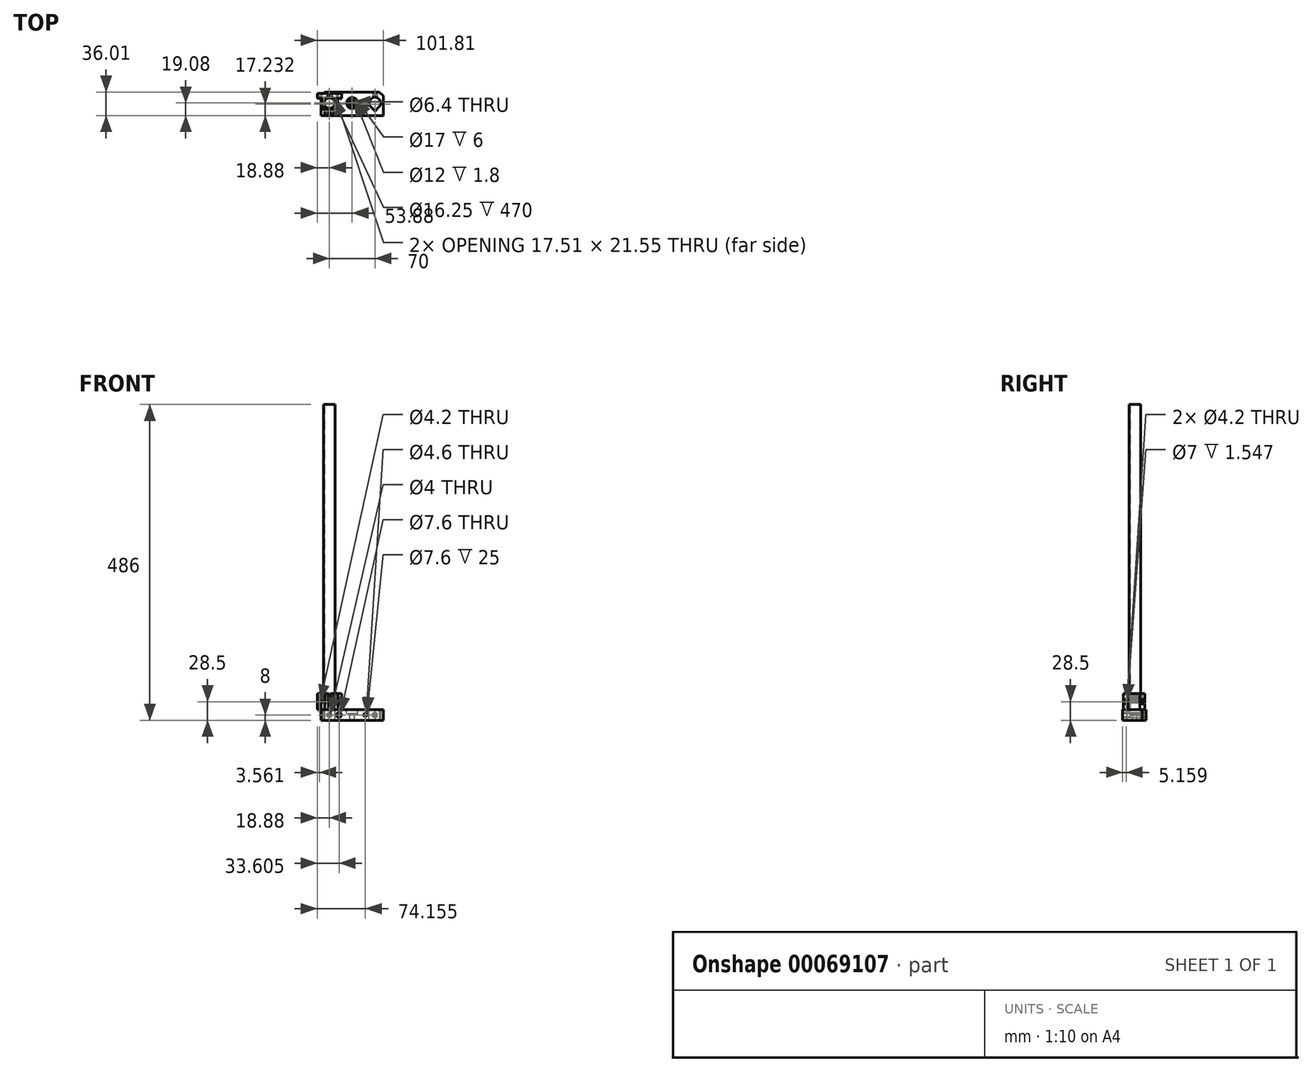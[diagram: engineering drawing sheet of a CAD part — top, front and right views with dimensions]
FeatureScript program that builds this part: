
annotation { "Feature Type Name" : "Feature", "Feature Type Description" : "" }
export const myFeature = defineFeature(function(context is Context, id is Id, definition is map)
    precondition{}
    {
        {
            var Q0;
            Q0=qCreatedBy(makeId("Top.planeOp"),FACE);
            var sketch = newSketch(context, id + "F0", { "sketchPlane" : qUnion([Q0])});
            skCircle(sketch, "E0", {"center": v(0, 0) * mm, "radius": 8.93 * mm, "construction": true});
            skLineSegment(sketch, "E1", {"start": v(0, 0) * mm, "end": v(0, 15.23) * mm, "construction": true});
            skLineSegment(sketch, "E2", {"start": v(0, 15.23) * mm, "end": v(18.88, 15.23) * mm});
            skLineSegment(sketch, "E3", {"start": v(18.88, 15.23) * mm, "end": v(18.88, 7.23) * mm});
            skLineSegment(sketch, "E4", {"start": v(18.88, 7.23) * mm, "end": v(11.08, 7.23) * mm});
            skArc(sketch, "E5", {"start": v(3.5, -8.54) * mm, "mid": v(9.05, 1.78) * mm, "end": v(0, 9.23) * mm});
            skArc(sketch, "E6", {"start": v(7, -11.22) * mm, "mid": v(12.91, -2.85) * mm, "end": v(11.08, 7.23) * mm});
            skLineSegment(sketch, "E7", {"start": v(1.5, -10.21) * mm, "end": v(1.5, -18.02) * mm});
            skLineSegment(sketch, "E8", {"start": v(1.5, -18.02) * mm, "end": v(7, -18.02) * mm});
            skLineSegment(sketch, "E9", {"start": v(7, -18.02) * mm, "end": v(7, -11.22) * mm});
            skLineSegment(sketch, "E10", {"start": v(1.5, -10.21) * mm, "end": v(3.5, -8.54) * mm});
            skLineSegment(sketch, "E11.MirrorCS", {"start": v(-1.5, -10.21) * mm, "end": v(-3.5, -8.54) * mm});
            skLineSegment(sketch, "E12.MirrorCS", {"start": v(-7, -18.02) * mm, "end": v(-7, -11.22) * mm});
            skLineSegment(sketch, "E13.MirrorCS", {"start": v(-1.5, -18.02) * mm, "end": v(-7, -18.02) * mm});
            skLineSegment(sketch, "E14.MirrorCS", {"start": v(-18.88, 7.22) * mm, "end": v(-11.08, 7.22) * mm});
            skLineSegment(sketch, "E15.MirrorCS", {"start": v(-18.88, 15.23) * mm, "end": v(-18.88, 7.22) * mm});
            skLineSegment(sketch, "E16.MirrorCS", {"start": v(0, 15.23) * mm, "end": v(-18.88, 15.22) * mm});
            skLineSegment(sketch, "E17.MirrorCS", {"start": v(-1.5, -10.21) * mm, "end": v(-1.5, -18.02) * mm});
            skArc(sketch, "E18.MirrorCS", {"start": v(-7, -11.22) * mm, "mid": v(-12.91, -2.85) * mm, "end": v(-11.08, 7.22) * mm});
            skArc(sketch, "E19.MirrorCS", {"start": v(-3.5, -8.54) * mm, "mid": v(-9.05, 1.78) * mm, "end": v(0, 9.23) * mm});
            skLineSegment(sketch, "E20.bottom", {"start": v(-10.53, 0.4) * mm, "end": v(-7.32, 0.4) * mm});
            skLineSegment(sketch, "E20.top", {"start": v(-10.53, -0.4) * mm, "end": v(-7.32, -0.4) * mm});
            skLineSegment(sketch, "E20.left", {"start": v(-10.53, 0.4) * mm, "end": v(-10.53, -0.4) * mm});
            skLineSegment(sketch, "E20.right", {"start": v(-7.33, 0.4) * mm, "end": v(-7.33, -0.4) * mm});
            skPoint(sketch, "E20.middle", {"position": v(-8.93, 0) * mm});
            skLineSegment(sketch, "E21.1.0", {"start": v(-10.27, -2.34) * mm, "end": v(-10.06, -3.11) * mm});
            skLineSegment(sketch, "E21.1.1", {"start": v(-10.27, -2.34) * mm, "end": v(-7.18, -1.5) * mm});
            skLineSegment(sketch, "E21.1.2", {"start": v(-7.18, -1.5) * mm, "end": v(-6.97, -2.28) * mm});
            skLineSegment(sketch, "E21.1.3", {"start": v(-10.06, -3.11) * mm, "end": v(-6.97, -2.28) * mm});
            skLineSegment(sketch, "E21.2.0", {"start": v(-9.31, -4.92) * mm, "end": v(-8.91, -5.6) * mm});
            skLineSegment(sketch, "E21.2.1", {"start": v(-9.31, -4.92) * mm, "end": v(-6.54, -3.32) * mm});
            skLineSegment(sketch, "E21.2.2", {"start": v(-6.54, -3.32) * mm, "end": v(-6.14, -4) * mm});
            skLineSegment(sketch, "E21.2.3", {"start": v(-8.91, -5.6) * mm, "end": v(-6.14, -4) * mm});
            skLineSegment(sketch, "E21.3.0", {"start": v(-7.73, -7.16) * mm, "end": v(-7.16, -7.73) * mm});
            skLineSegment(sketch, "E21.3.1", {"start": v(-7.73, -7.16) * mm, "end": v(-5.46, -4.9) * mm});
            skLineSegment(sketch, "E21.3.2", {"start": v(-5.46, -4.9) * mm, "end": v(-4.9, -5.46) * mm});
            skLineSegment(sketch, "E21.3.3", {"start": v(-7.16, -7.73) * mm, "end": v(-4.9, -5.46) * mm});
            skLineSegment(sketch, "E21.4.0", {"start": v(-5.6, -8.91) * mm, "end": v(-4.92, -9.31) * mm});
            skLineSegment(sketch, "E21.4.1", {"start": v(-5.6, -8.91) * mm, "end": v(-4, -6.14) * mm});
            skLineSegment(sketch, "E21.4.2", {"start": v(-4, -6.14) * mm, "end": v(-3.32, -6.54) * mm});
            skLineSegment(sketch, "E21.4.3", {"start": v(-4.92, -9.31) * mm, "end": v(-3.32, -6.54) * mm});
            skLineSegment(sketch, "E21.5.0", {"start": v(-3.11, -10.06) * mm, "end": v(-2.34, -10.27) * mm, "construction": true});
            skLineSegment(sketch, "E21.5.1", {"start": v(-3.11, -10.06) * mm, "end": v(-2.28, -6.97) * mm, "construction": true});
            skLineSegment(sketch, "E21.5.2", {"start": v(-2.28, -6.97) * mm, "end": v(-1.5, -7.18) * mm, "construction": true});
            skLineSegment(sketch, "E21.5.3", {"start": v(-2.34, -10.27) * mm, "end": v(-1.5, -7.18) * mm, "construction": true});
            skLineSegment(sketch, "E21.6.0", {"start": v(-0.4, -10.53) * mm, "end": v(0.4, -10.53) * mm, "construction": true});
            skLineSegment(sketch, "E21.6.1", {"start": v(-0.4, -10.53) * mm, "end": v(-0.4, -7.33) * mm, "construction": true});
            skLineSegment(sketch, "E21.6.2", {"start": v(-0.4, -7.33) * mm, "end": v(0.4, -7.33) * mm, "construction": true});
            skLineSegment(sketch, "E21.6.3", {"start": v(0.4, -10.53) * mm, "end": v(0.4, -7.32) * mm, "construction": true});
            skLineSegment(sketch, "E21.7.0", {"start": v(2.34, -10.27) * mm, "end": v(3.11, -10.06) * mm, "construction": true});
            skLineSegment(sketch, "E21.7.1", {"start": v(2.34, -10.27) * mm, "end": v(1.5, -7.18) * mm, "construction": true});
            skLineSegment(sketch, "E21.7.2", {"start": v(1.5, -7.18) * mm, "end": v(2.28, -6.97) * mm, "construction": true});
            skLineSegment(sketch, "E21.7.3", {"start": v(3.11, -10.06) * mm, "end": v(2.28, -6.97) * mm, "construction": true});
            skLineSegment(sketch, "E21.8.0", {"start": v(4.92, -9.31) * mm, "end": v(5.6, -8.91) * mm});
            skLineSegment(sketch, "E21.8.1", {"start": v(4.92, -9.31) * mm, "end": v(3.32, -6.54) * mm});
            skLineSegment(sketch, "E21.8.2", {"start": v(3.32, -6.54) * mm, "end": v(4, -6.14) * mm});
            skLineSegment(sketch, "E21.8.3", {"start": v(5.6, -8.91) * mm, "end": v(4, -6.14) * mm});
            skLineSegment(sketch, "E21.9.0", {"start": v(7.16, -7.73) * mm, "end": v(7.73, -7.16) * mm});
            skLineSegment(sketch, "E21.9.1", {"start": v(7.16, -7.73) * mm, "end": v(4.9, -5.46) * mm});
            skLineSegment(sketch, "E21.9.2", {"start": v(4.9, -5.46) * mm, "end": v(5.46, -4.9) * mm});
            skLineSegment(sketch, "E21.9.3", {"start": v(7.73, -7.16) * mm, "end": v(5.46, -4.9) * mm});
            skLineSegment(sketch, "E21.10.0", {"start": v(8.91, -5.6) * mm, "end": v(9.31, -4.92) * mm});
            skLineSegment(sketch, "E21.10.1", {"start": v(8.91, -5.6) * mm, "end": v(6.14, -4) * mm});
            skLineSegment(sketch, "E21.10.2", {"start": v(6.14, -4) * mm, "end": v(6.54, -3.32) * mm});
            skLineSegment(sketch, "E21.10.3", {"start": v(9.31, -4.92) * mm, "end": v(6.54, -3.32) * mm});
            skLineSegment(sketch, "E21.11.0", {"start": v(10.06, -3.11) * mm, "end": v(10.27, -2.34) * mm});
            skLineSegment(sketch, "E21.11.1", {"start": v(10.06, -3.11) * mm, "end": v(6.97, -2.28) * mm});
            skLineSegment(sketch, "E21.11.2", {"start": v(6.97, -2.28) * mm, "end": v(7.18, -1.5) * mm});
            skLineSegment(sketch, "E21.11.3", {"start": v(10.27, -2.34) * mm, "end": v(7.18, -1.5) * mm});
            skLineSegment(sketch, "E21.12.0", {"start": v(10.53, -0.4) * mm, "end": v(10.53, 0.4) * mm});
            skLineSegment(sketch, "E21.12.1", {"start": v(10.53, -0.4) * mm, "end": v(7.33, -0.4) * mm});
            skLineSegment(sketch, "E21.12.2", {"start": v(7.33, -0.4) * mm, "end": v(7.33, 0.4) * mm});
            skLineSegment(sketch, "E21.12.3", {"start": v(10.53, 0.4) * mm, "end": v(7.32, 0.4) * mm});
            skLineSegment(sketch, "E21.13.0", {"start": v(10.27, 2.34) * mm, "end": v(10.06, 3.11) * mm});
            skLineSegment(sketch, "E21.13.1", {"start": v(10.27, 2.34) * mm, "end": v(7.18, 1.5) * mm});
            skLineSegment(sketch, "E21.13.2", {"start": v(7.18, 1.5) * mm, "end": v(6.97, 2.28) * mm});
            skLineSegment(sketch, "E21.13.3", {"start": v(10.06, 3.11) * mm, "end": v(6.97, 2.28) * mm});
            skLineSegment(sketch, "E21.14.0", {"start": v(9.31, 4.92) * mm, "end": v(8.91, 5.6) * mm});
            skLineSegment(sketch, "E21.14.1", {"start": v(9.31, 4.92) * mm, "end": v(6.54, 3.32) * mm});
            skLineSegment(sketch, "E21.14.2", {"start": v(6.54, 3.32) * mm, "end": v(6.14, 4) * mm});
            skLineSegment(sketch, "E21.14.3", {"start": v(8.91, 5.6) * mm, "end": v(6.14, 4) * mm});
            skLineSegment(sketch, "E21.15.0", {"start": v(7.73, 7.16) * mm, "end": v(7.16, 7.73) * mm});
            skLineSegment(sketch, "E21.15.1", {"start": v(7.73, 7.16) * mm, "end": v(5.46, 4.9) * mm});
            skLineSegment(sketch, "E21.15.2", {"start": v(5.46, 4.9) * mm, "end": v(4.9, 5.46) * mm});
            skLineSegment(sketch, "E21.15.3", {"start": v(7.16, 7.73) * mm, "end": v(4.9, 5.46) * mm});
            skLineSegment(sketch, "E21.16.0", {"start": v(5.6, 8.91) * mm, "end": v(4.92, 9.31) * mm});
            skLineSegment(sketch, "E21.16.1", {"start": v(5.6, 8.91) * mm, "end": v(4, 6.14) * mm});
            skLineSegment(sketch, "E21.16.2", {"start": v(4, 6.14) * mm, "end": v(3.32, 6.54) * mm});
            skLineSegment(sketch, "E21.16.3", {"start": v(4.92, 9.31) * mm, "end": v(3.32, 6.54) * mm});
            skLineSegment(sketch, "E21.17.0", {"start": v(3.11, 10.06) * mm, "end": v(2.34, 10.27) * mm});
            skLineSegment(sketch, "E21.17.1", {"start": v(3.11, 10.06) * mm, "end": v(2.28, 6.97) * mm});
            skLineSegment(sketch, "E21.17.2", {"start": v(2.28, 6.97) * mm, "end": v(1.5, 7.18) * mm});
            skLineSegment(sketch, "E21.17.3", {"start": v(2.34, 10.27) * mm, "end": v(1.5, 7.18) * mm});
            skLineSegment(sketch, "E21.18.0", {"start": v(0.4, 10.53) * mm, "end": v(-0.4, 10.53) * mm});
            skLineSegment(sketch, "E21.18.1", {"start": v(0.4, 10.53) * mm, "end": v(0.4, 7.33) * mm});
            skLineSegment(sketch, "E21.18.2", {"start": v(0.4, 7.33) * mm, "end": v(-0.4, 7.33) * mm});
            skLineSegment(sketch, "E21.18.3", {"start": v(-0.4, 10.53) * mm, "end": v(-0.4, 7.32) * mm});
            skLineSegment(sketch, "E21.19.0", {"start": v(-2.34, 10.27) * mm, "end": v(-3.11, 10.06) * mm});
            skLineSegment(sketch, "E21.19.1", {"start": v(-2.34, 10.27) * mm, "end": v(-1.5, 7.18) * mm});
            skLineSegment(sketch, "E21.19.2", {"start": v(-1.5, 7.18) * mm, "end": v(-2.28, 6.97) * mm});
            skLineSegment(sketch, "E21.19.3", {"start": v(-3.11, 10.06) * mm, "end": v(-2.28, 6.97) * mm});
            skLineSegment(sketch, "E21.20.0", {"start": v(-4.92, 9.31) * mm, "end": v(-5.6, 8.91) * mm});
            skLineSegment(sketch, "E21.20.1", {"start": v(-4.92, 9.31) * mm, "end": v(-3.32, 6.54) * mm});
            skLineSegment(sketch, "E21.20.2", {"start": v(-3.32, 6.54) * mm, "end": v(-4, 6.14) * mm});
            skLineSegment(sketch, "E21.20.3", {"start": v(-5.6, 8.91) * mm, "end": v(-4, 6.14) * mm});
            skLineSegment(sketch, "E21.21.0", {"start": v(-7.16, 7.73) * mm, "end": v(-7.73, 7.16) * mm});
            skLineSegment(sketch, "E21.21.1", {"start": v(-7.16, 7.73) * mm, "end": v(-4.9, 5.46) * mm});
            skLineSegment(sketch, "E21.21.2", {"start": v(-4.9, 5.46) * mm, "end": v(-5.46, 4.9) * mm});
            skLineSegment(sketch, "E21.21.3", {"start": v(-7.73, 7.16) * mm, "end": v(-5.46, 4.9) * mm});
            skLineSegment(sketch, "E21.22.0", {"start": v(-8.91, 5.6) * mm, "end": v(-9.31, 4.92) * mm});
            skLineSegment(sketch, "E21.22.1", {"start": v(-8.91, 5.6) * mm, "end": v(-6.14, 4) * mm});
            skLineSegment(sketch, "E21.22.2", {"start": v(-6.14, 4) * mm, "end": v(-6.54, 3.32) * mm});
            skLineSegment(sketch, "E21.22.3", {"start": v(-9.31, 4.92) * mm, "end": v(-6.54, 3.32) * mm});
            skLineSegment(sketch, "E21.23.0", {"start": v(-10.06, 3.11) * mm, "end": v(-10.27, 2.34) * mm});
            skLineSegment(sketch, "E21.23.1", {"start": v(-10.06, 3.11) * mm, "end": v(-6.97, 2.28) * mm});
            skLineSegment(sketch, "E21.23.2", {"start": v(-6.97, 2.28) * mm, "end": v(-7.18, 1.5) * mm});
            skLineSegment(sketch, "E21.23.3", {"start": v(-10.27, 2.34) * mm, "end": v(-7.18, 1.5) * mm});
            skSolve(sketch);
        }
        {
            var Q0;
            Q0=makeQuery(id+"F0.imprint","IMPRINT",FACE,{"disambiguationData":[TD([[makeQuery(id+"F0.imprint","IMPRINT",EDGE,{"derivedFrom":sQuery(id+"F0.wireOp",EDGE,"E2")}),-1.0]])]});
            extrude(context, id + "F1", {"entities" : qUnion([Q0]), "depth" : 25 * mm, "offsetDistance" : 25 * mm});
        }
        {
            var Q0;
            Q0=makeQuery(id+"F1.opExtrude","SWEPT_FACE",FACE,{"disambiguationData":[OSD([sQuery(id+"F0.wireOp",EDGE,"E12.MirrorCS")])]});
            var sketch = newSketch(context, id + "F2", { "sketchPlane" : qUnion([Q0])});
            skCircle(sketch, "E22", {"center": v(13.92, 12.5) * mm, "radius": 2.1 * mm});
            skPoint(sketch, "E22.centerSnap0", {"position": v(18.02, 12.5) * mm});
            skCircle(sketch, "E23.cCircle", {"center": v(13.92, 12.5) * mm, "radius": 3.5 * mm, "construction": true});
            skLineSegment(sketch, "E23.0", {"start": v(17.42, 14.52) * mm, "end": v(17.42, 10.48) * mm});
            skLineSegment(sketch, "E23.1", {"start": v(17.42, 10.48) * mm, "end": v(13.92, 8.46) * mm});
            skLineSegment(sketch, "E23.2", {"start": v(13.92, 8.46) * mm, "end": v(10.42, 10.48) * mm});
            skLineSegment(sketch, "E23.3", {"start": v(10.42, 10.48) * mm, "end": v(10.42, 14.52) * mm});
            skLineSegment(sketch, "E23.4", {"start": v(10.42, 14.52) * mm, "end": v(13.92, 16.54) * mm});
            skLineSegment(sketch, "E23.5", {"start": v(13.92, 16.54) * mm, "end": v(17.42, 14.52) * mm});
            skPoint(sketch, "E23.0.midPoint", {"position": v(17.42, 12.5) * mm});
            skSolve(sketch);
        }
        {
            var Q0;
            Q0=makeQuery(id+"F2.imprint","IMPRINT",FACE,{"disambiguationData":[TD([[makeQuery(id+"F2.imprint","IMPRINT",EDGE,{"derivedFrom":sQuery(id+"F2.wireOp",EDGE,"E22")}),1.0]])]});
            extrude(context, id + "F3", {"entities" : qUnion([Q0]), "operationType" : NewBodyOperationType.REMOVE, "endBound" : BoundingType.THROUGH_ALL, "oppositeDirection" : true, "depth" : 25 * mm, "offsetDistance" : 25 * mm});
        }
        {
            var Q0;
            {var subQ0=sQuery(id+"F2.wireOp",EDGE,"E23.3");Q0=makeQuery(id+"F2.imprint","IMPRINT",FACE,{"disambiguationData":[TD([[makeQuery(id+"F2.imprint","IMPRINT",EDGE,{"derivedFrom":subQ0}),-1.0]])]});}
            var Q1;
            Q1=makeQuery(id+"F2.imprint","IMPRINT",FACE,{"disambiguationData":[TD([[makeQuery(id+"F2.imprint","IMPRINT",EDGE,{"derivedFrom":sQuery(id+"F2.wireOp",EDGE,"E22")}),-1.0]])]});
            extrude(context, id + "F4", {"entities" : qUnion([Q0, Q1]), "operationType" : NewBodyOperationType.REMOVE, "oppositeDirection" : true, "depth" : 2 * mm, "offsetDistance" : 25 * mm, "hasSecondDirection" : true, "secondDirectionBound" : BoundingType.THROUGH_ALL, "secondDirectionOppositeDirection" : false, "secondDirectionDepth" : 25 * mm});
        }
        {
            var Q0;
            Q0=makeQuery(id+"F1.opExtrude","SWEPT_FACE",FACE,{"disambiguationData":[OSD([sQuery(id+"F0.wireOp",EDGE,"E9")])]});
            var sketch = newSketch(context, id + "F5", { "sketchPlane" : qUnion([Q0])});
            skCircle(sketch, "E24", {"center": v(-13.92, 12.5) * mm, "radius": 3.5 * mm});
            skSolve(sketch);
        }
        {
            var Q0;
            Q0 = qSketchRegion(id + "F5", true);
            extrude(context, id + "F6", {"entities" : qUnion([Q0]), "operationType" : NewBodyOperationType.REMOVE, "oppositeDirection" : true, "depth" : 0.4 * mm, "offsetDistance" : 25 * mm, "hasSecondDirection" : true, "secondDirectionBound" : BoundingType.THROUGH_ALL, "secondDirectionOppositeDirection" : false, "secondDirectionDepth" : 25 * mm});
        }
        {
            var Q0;
            Q0=makeQuery(id+"F1.opExtrude","SWEPT_FACE",FACE,{"disambiguationData":[OSD([sQuery(id+"F0.wireOp",EDGE,"E4")])]});
            var sketch = newSketch(context, id + "F7", { "sketchPlane" : qUnion([Q0])});
            skLineSegment(sketch, "E25", {"start": v(18.88, 12.5) * mm, "end": v(-18.88, 12.5) * mm, "construction": true});
            skCircle(sketch, "E26.cCircle", {"center": v(-15.32, 12.5) * mm, "radius": 3.5 * mm, "construction": true});
            skLineSegment(sketch, "E26.0", {"start": v(-13.3, 9) * mm, "end": v(-17.34, 9) * mm});
            skLineSegment(sketch, "E26.1", {"start": v(-17.34, 9) * mm, "end": v(-19.36, 12.5) * mm, "construction": true});
            skLineSegment(sketch, "E26.2", {"start": v(-19.36, 12.5) * mm, "end": v(-17.34, 16) * mm, "construction": true});
            skLineSegment(sketch, "E26.3", {"start": v(-17.34, 16) * mm, "end": v(-13.3, 16) * mm});
            skLineSegment(sketch, "E26.4", {"start": v(-13.3, 16) * mm, "end": v(-11.28, 12.5) * mm});
            skLineSegment(sketch, "E26.5", {"start": v(-11.28, 12.5) * mm, "end": v(-13.3, 9) * mm});
            skPoint(sketch, "E26.0.midPoint", {"position": v(-15.32, 9) * mm});
            skLineSegment(sketch, "E27", {"start": v(-17.34, 16) * mm, "end": v(-18.88, 16) * mm});
            skLineSegment(sketch, "E28", {"start": v(-18.88, 16) * mm, "end": v(-18.88, 9) * mm});
            skLineSegment(sketch, "E29", {"start": v(-18.88, 9) * mm, "end": v(-17.34, 9) * mm});
            skCircle(sketch, "E30", {"center": v(-15.32, 12.5) * mm, "radius": 2.1 * mm});
            skPoint(sketch, "E31.0", {"position": v(0, 0) * mm});
            skLineSegment(sketch, "E32", {"start": v(0, 0) * mm, "end": v(0, 12.5) * mm, "construction": true});
            skLineSegment(sketch, "E33.MirrorCS", {"start": v(18.88, 9) * mm, "end": v(17.34, 9) * mm});
            skLineSegment(sketch, "E34.MirrorCS", {"start": v(17.34, 16) * mm, "end": v(18.88, 16) * mm});
            skLineSegment(sketch, "E35.MirrorCS", {"start": v(13.3, 16) * mm, "end": v(11.28, 12.5) * mm});
            skLineSegment(sketch, "E36.MirrorCS", {"start": v(18.88, 16) * mm, "end": v(18.88, 9) * mm});
            skLineSegment(sketch, "E37.MirrorCS", {"start": v(19.36, 12.5) * mm, "end": v(17.34, 16) * mm, "construction": true});
            skLineSegment(sketch, "E38.MirrorCS", {"start": v(17.34, 9) * mm, "end": v(19.36, 12.5) * mm, "construction": true});
            skLineSegment(sketch, "E39.MirrorCS", {"start": v(11.28, 12.5) * mm, "end": v(13.3, 9) * mm});
            skLineSegment(sketch, "E40.MirrorCS", {"start": v(13.3, 9) * mm, "end": v(17.34, 9) * mm});
            skLineSegment(sketch, "E41.MirrorCS", {"start": v(17.34, 16) * mm, "end": v(13.3, 16) * mm});
            skPoint(sketch, "E42.MirrorP", {"position": v(15.32, 9) * mm});
            skCircle(sketch, "E43.MirrorC", {"center": v(15.32, 12.5) * mm, "radius": 3.5 * mm, "construction": true});
            skCircle(sketch, "E44.MirrorC", {"center": v(15.32, 12.5) * mm, "radius": 2.1 * mm});
            skSolve(sketch);
        }
        {
            var Q0;
            Q0 = qSketchRegion(id + "F7", true);
            extrude(context, id + "F8", {"entities" : qUnion([Q0]), "operationType" : NewBodyOperationType.REMOVE, "oppositeDirection" : true, "depth" : 3.2 * mm, "offsetDistance" : 25 * mm});
        }
        {
            var Q0;
            Q0=makeQuery(id+"F7.imprint","IMPRINT",FACE,{"disambiguationData":[TD([[makeQuery(id+"F7.imprint","IMPRINT",EDGE,{"derivedFrom":sQuery(id+"F7.wireOp",EDGE,"E30")}),1.0]])]});
            var Q1;
            Q1=makeQuery(id+"F7.imprint","IMPRINT",FACE,{"disambiguationData":[TD([[makeQuery(id+"F7.imprint","IMPRINT",EDGE,{"derivedFrom":sQuery(id+"F7.wireOp",EDGE,"E44.MirrorC")}),-1.0]])]});
            extrude(context, id + "F9", {"entities" : qUnion([Q0, Q1]), "operationType" : NewBodyOperationType.REMOVE, "endBound" : BoundingType.THROUGH_ALL, "oppositeDirection" : true, "depth" : 25 * mm, "offsetDistance" : 25 * mm});
        }
        {
            var Q0;
            Q0=qCreatedBy(makeId("Top.planeOp"),FACE);
            var sketch = newSketch(context, id + "F10", { "sketchPlane" : qUnion([Q0])});
            skCircle(sketch, "E45.0", {"center": v(0, 0) * mm, "radius": 8.93 * mm});
            skLineSegment(sketch, "E46", {"start": v(35, 0) * mm, "end": v(35, -63.16) * mm, "construction": true});
            skLineSegment(sketch, "E47", {"start": v(35, -19.08) * mm, "end": v(-12.93, -19.08) * mm});
            skLineSegment(sketch, "E48", {"start": v(-12.93, -19.08) * mm, "end": v(-12.93, 16.92) * mm});
            skLineSegment(sketch, "E49", {"start": v(-12.93, 16.92) * mm, "end": v(35, 16.93) * mm});
            skLineSegment(sketch, "E50", {"start": v(6.31, -6.31) * mm, "end": v(0, -12.62) * mm});
            skLineSegment(sketch, "E51", {"start": v(0, 0) * mm, "end": v(0, -12.62) * mm, "construction": true});
            skLineSegment(sketch, "E52.MirrorCS", {"start": v(-6.31, -6.31) * mm, "end": v(0, -12.62) * mm});
            skLineSegment(sketch, "E53.MirrorCS", {"start": v(35, -19.07) * mm, "end": v(82.93, -19.07) * mm});
            skLineSegment(sketch, "E54.MirrorCS", {"start": v(82.93, -19.07) * mm, "end": v(82.93, 16.93) * mm});
            skLineSegment(sketch, "E55.MirrorCS", {"start": v(82.92, 16.93) * mm, "end": v(35, 16.93) * mm});
            skLineSegment(sketch, "E56.MirrorCS", {"start": v(63.69, -6.31) * mm, "end": v(70, -12.62) * mm});
            skLineSegment(sketch, "E57.MirrorCS", {"start": v(76.31, -6.31) * mm, "end": v(70, -12.62) * mm});
            skCircle(sketch, "E58.MirrorC", {"center": v(70, 0) * mm, "radius": 8.93 * mm});
            skCircle(sketch, "E59", {"center": v(35, 0) * mm, "radius": 3.2 * mm});
            skCircle(sketch, "E60", {"center": v(35, 0) * mm, "radius": 8.5 * mm});
            skSolve(sketch);
        }
        {
            var Q0;
            Q0=makeQuery(id+"F10.imprint","IMPRINT",FACE,{"disambiguationData":[TD([[makeQuery(id+"F10.imprint","IMPRINT",EDGE,{"derivedFrom":sQuery(id+"F10.wireOp",EDGE,"E47")}),-1.0]])]});
            var Q1;
            Q1=makeQuery(id+"F10.imprint","IMPRINT",FACE,{"disambiguationData":[TD([[makeQuery(id+"F10.imprint","IMPRINT",EDGE,{"derivedFrom":sQuery(id+"F10.wireOp",EDGE,"E59")}),-1.0]])]});
            extrude(context, id + "F11", {"entities" : qUnion([Q0, Q1]), "oppositeDirection" : true, "depth" : 16 * mm, "offsetDistance" : 25 * mm});
        }
        {
            var Q0;
            Q0=makeQuery(id+"F11.opExtrude","SWEPT_EDGE",EDGE,{"disambiguationData":[OSD([sQuery(id+"F10.wireOp",EDGE,"E48"),sQuery(id+"F10.wireOp",EDGE,"E49")])]});
            var Q1;
            Q1=makeQuery(id+"F11.opExtrude","SWEPT_EDGE",EDGE,{"disambiguationData":[OSD([sQuery(id+"F10.wireOp",EDGE,"E54.MirrorCS"),sQuery(id+"F10.wireOp",EDGE,"E55.MirrorCS")])]});
            chamfer(context, id + "F12", {"entities" : qUnion([Q0, Q1]), "width" : 6 * mm, "tangentPropagation" : true});
        }
        {
            var Q0;
            Q0=makeQuery(id+"F10.imprint","IMPRINT",FACE,{"disambiguationData":[TD([[makeQuery(id+"F10.imprint","IMPRINT",EDGE,{"derivedFrom":sQuery(id+"F10.wireOp",EDGE,"E59")}),-1.0]])]});
            extrude(context, id + "F13", {"entities" : qUnion([Q0]), "operationType" : NewBodyOperationType.REMOVE, "oppositeDirection" : true, "depth" : 6 * mm, "offsetDistance" : 25 * mm});
        }
        {
            var Q0;
            Q0=makeQuery(id+"F13.boolean.opBoolean","COPY",FACE,{"derivedFrom":makeQuery(id+"F13.opExtrude","CAP_FACE",FACE,{"disambiguationData":[OSD([sQuery(id+"F10.wireOp",EDGE,"E59"),sQuery(id+"F10.wireOp",EDGE,"E60")])],"isStart":false})});
            var sketch = newSketch(context, id + "F14", { "sketchPlane" : qUnion([Q0])});
            skCircle(sketch, "E61", {"center": v(35, 0) * mm, "radius": 6 * mm});
            skSolve(sketch);
        }
        {
            var Q0;
            Q0 = qSketchRegion(id + "F14", true);
            extrude(context, id + "F15", {"entities" : qUnion([Q0]), "operationType" : NewBodyOperationType.REMOVE, "oppositeDirection" : true, "depth" : 1.8 * mm, "offsetDistance" : 25 * mm});
        }
        {
            var Q0;
            Q0=qCreatedBy(makeId("Front.planeOp"),FACE);
            var sketch = newSketch(context, id + "F16", { "sketchPlane" : qUnion([Q0])});
            skPoint(sketch, "E62.0", {"position": v(-12.93, -8) * mm});
            skPoint(sketch, "E63.0", {"position": v(35, -16) * mm});
            skLineSegment(sketch, "E64", {"start": v(35, -16) * mm, "end": v(35, 0) * mm, "construction": true});
            skCircle(sketch, "E65.cCircle", {"center": v(0, -8) * mm, "radius": 3.5 * mm, "construction": true});
            skLineSegment(sketch, "E65.0", {"start": v(-3.5, -10.02) * mm, "end": v(-3.5, -5.98) * mm});
            skLineSegment(sketch, "E65.1", {"start": v(-3.5, -5.98) * mm, "end": v(0, -3.96) * mm});
            skLineSegment(sketch, "E65.2", {"start": v(0, -3.96) * mm, "end": v(3.5, -5.98) * mm});
            skLineSegment(sketch, "E65.3", {"start": v(3.5, -5.98) * mm, "end": v(3.5, -10.02) * mm});
            skLineSegment(sketch, "E65.4", {"start": v(3.5, -10.02) * mm, "end": v(0, -12.04) * mm});
            skLineSegment(sketch, "E65.5", {"start": v(0, -12.04) * mm, "end": v(-3.5, -10.02) * mm});
            skPoint(sketch, "E65.0.midPoint", {"position": v(-3.5, -8) * mm});
            skCircle(sketch, "E66", {"center": v(0, -8) * mm, "radius": 2 * mm});
            skLineSegment(sketch, "E67.MirrorCS", {"start": v(73.5, -10.02) * mm, "end": v(73.5, -5.98) * mm});
            skLineSegment(sketch, "E68.MirrorCS", {"start": v(73.5, -5.98) * mm, "end": v(70, -3.96) * mm});
            skLineSegment(sketch, "E69.MirrorCS", {"start": v(70, -12.04) * mm, "end": v(73.5, -10.02) * mm});
            skLineSegment(sketch, "E70.MirrorCS", {"start": v(66.5, -5.98) * mm, "end": v(66.5, -10.02) * mm});
            skCircle(sketch, "E71.MirrorC", {"center": v(70, -8) * mm, "radius": 2 * mm});
            skLineSegment(sketch, "E72.MirrorCS", {"start": v(70, -3.96) * mm, "end": v(66.5, -5.98) * mm});
            skLineSegment(sketch, "E73.MirrorCS", {"start": v(66.5, -10.02) * mm, "end": v(70, -12.04) * mm});
            skPoint(sketch, "E74.MirrorP", {"position": v(73.5, -8) * mm});
            skCircle(sketch, "E75.MirrorC", {"center": v(70, -8) * mm, "radius": 3.5 * mm, "construction": true});
            skSolve(sketch);
        }
        {
            var Q0;
            Q0=makeQuery(id+"F16.imprint","IMPRINT",FACE,{"disambiguationData":[TD([[makeQuery(id+"F16.imprint","IMPRINT",EDGE,{"derivedFrom":sQuery(id+"F16.wireOp",EDGE,"E71.MirrorC")}),-1.0]])]});
            var Q1;
            Q1=makeQuery(id+"F16.imprint","IMPRINT",FACE,{"disambiguationData":[TD([[makeQuery(id+"F16.imprint","IMPRINT",EDGE,{"derivedFrom":sQuery(id+"F16.wireOp",EDGE,"E66")}),1.0]])]});
            extrude(context, id + "F17", {"entities" : qUnion([Q0, Q1]), "operationType" : NewBodyOperationType.REMOVE, "endBound" : BoundingType.THROUGH_ALL, "oppositeDirection" : true, "depth" : 25 * mm, "offsetDistance" : 25 * mm});
        }
        {
            var Q0;
            Q0=makeQuery(id+"F16.imprint","IMPRINT",FACE,{"disambiguationData":[TD([[makeQuery(id+"F16.imprint","IMPRINT",EDGE,{"derivedFrom":sQuery(id+"F16.wireOp",EDGE,"E67.MirrorCS")}),1.0]])]});
            var Q1;
            Q1=makeQuery(id+"F16.imprint","IMPRINT",FACE,{"disambiguationData":[TD([[makeQuery(id+"F16.imprint","IMPRINT",EDGE,{"derivedFrom":sQuery(id+"F16.wireOp",EDGE,"E65.0")}),-1.0]])]});
            extrude(context, id + "F18", {"entities" : qUnion([Q0, Q1]), "operationType" : NewBodyOperationType.REMOVE, "oppositeDirection" : true, "depth" : (8.9 + 3.2 + .2) * mm, "offsetDistance" : 25 * mm});
        }
        {
            var Q0;
            Q0=makeQuery(id+"F11.opExtrude","SWEPT_FACE",FACE,{"disambiguationData":[OSD([sQuery(id+"F10.wireOp",EDGE,"E49"),sQuery(id+"F10.wireOp",EDGE,"E55.MirrorCS")])]});
            var sketch = newSketch(context, id + "F19", { "sketchPlane" : qUnion([Q0])});
            skLineSegment(sketch, "E76", {"start": v(-35, 0) * mm, "end": v(-35, -16) * mm, "construction": true});
            skCircle(sketch, "E77", {"center": v(-55.27, -8) * mm, "radius": 2.3 * mm});
            skPoint(sketch, "E77.centerSnap0", {"position": v(-35, -8) * mm});
            skCircle(sketch, "E78", {"center": v(-55.27, -8) * mm, "radius": 3.8 * mm});
            skLineSegment(sketch, "E79.0", {"start": v(-61.08, 0) * mm, "end": v(-78.93, 0) * mm, "construction": true});
            skLineSegment(sketch, "E80", {"start": v(-61.08, 0) * mm, "end": v(-61.08, -16) * mm, "construction": true});
            skCircle(sketch, "E81.MirrorC", {"center": v(-14.73, -8) * mm, "radius": 2.3 * mm});
            skCircle(sketch, "E82.MirrorC", {"center": v(-14.73, -8) * mm, "radius": 3.8 * mm});
            skSolve(sketch);
        }
        {
            var Q0;
            Q0=makeQuery(id+"F19.imprint","IMPRINT",FACE,{"disambiguationData":[TD([[makeQuery(id+"F19.imprint","IMPRINT",EDGE,{"derivedFrom":sQuery(id+"F19.wireOp",EDGE,"E77")}),1.0]])]});
            var Q1;
            Q1=makeQuery(id+"F19.imprint","IMPRINT",FACE,{"disambiguationData":[TD([[makeQuery(id+"F19.imprint","IMPRINT",EDGE,{"derivedFrom":sQuery(id+"F19.wireOp",EDGE,"E81.MirrorC")}),-1.0]])]});
            extrude(context, id + "F20", {"entities" : qUnion([Q0, Q1]), "operationType" : NewBodyOperationType.REMOVE, "endBound" : BoundingType.THROUGH_ALL, "oppositeDirection" : true, "depth" : 25 * mm, "offsetDistance" : 25 * mm});
        }
        {
            var Q0;
            Q0=makeQuery(id+"F19.imprint","IMPRINT",FACE,{"disambiguationData":[TD([[makeQuery(id+"F19.imprint","IMPRINT",EDGE,{"derivedFrom":sQuery(id+"F19.wireOp",EDGE,"E77")}),-1.0]])]});
            var Q1;
            Q1=makeQuery(id+"F19.imprint","IMPRINT",FACE,{"disambiguationData":[TD([[makeQuery(id+"F19.imprint","IMPRINT",EDGE,{"derivedFrom":sQuery(id+"F19.wireOp",EDGE,"E81.MirrorC")}),1.0]])]});
            extrude(context, id + "F21", {"entities" : qUnion([Q0, Q1]), "operationType" : NewBodyOperationType.REMOVE, "oppositeDirection" : true, "depth" : 25 * mm, "offsetDistance" : 25 * mm});
        }
        {
            var Q0;
            Q0=qCreatedBy(makeId("Top.planeOp"),FACE);
            var sketch = newSketch(context, id + "F22", { "sketchPlane" : qUnion([Q0])});
            skCircle(sketch, "E83.0", {"center": v(0, 0) * mm, "radius": 8.93 * mm});
            skCircle(sketch, "E84", {"center": v(0, 0) * mm, "radius": 8.12 * mm});
            skSolve(sketch);
        }
        {
            var Q0;
            Q0 = qSketchRegion(id + "F22", true);
            extrude(context, id + "F23", {"entities" : qUnion([Q0]), "depth" : 470 * mm, "offsetDistance" : 25 * mm});
        }
    });
